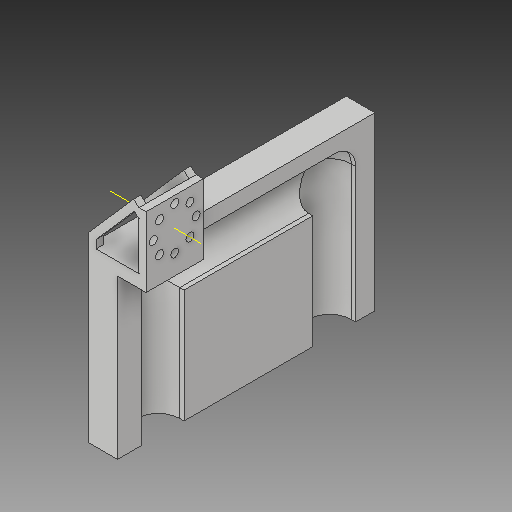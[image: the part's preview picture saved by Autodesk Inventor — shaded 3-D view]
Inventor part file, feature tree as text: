
AUTODESK INVENTOR PART (.ipt)
format: ipt  version: 2019 (Build 230136000, 136)  size: 240,128 bytes
history: native  units: in
note: dims shown in document units (in); Inventor stores cm internally (conversion verified against a paired STEP export)
features: sketch x7, extrude x6, projected_geometry x4, other x2, plane x1, mirror x1, pattern_circular x1, fillet x1
ambient origin geometry x8: Origin, YZ Plane, XZ Plane, XY Plane, X Axis, Y Axis, Z Axis, Center Point
bodies: Solid1 (feature_tree)
feature tree (23):
  other  "relicmold"
  extrude  "Extrusion1"  Depth=4.5in
  extrude  "Extrusion2"  Depth=1.0in
  extrude  "Extrusion3"  Depth=0.125in
  extrude  "Extrusion4"  Depth=0.125in
  plane  "Work Plane1"
  mirror  "Mirror1"
  extrude  "Extrusion5"  Depth=0.125in
  other  "Work Axis1"
  pattern_circular  "Circular Pattern1"  [2 undecoded]
  sketch  "Sketch6"  dims[d14=0.125in d15=0.0in]
  extrude  "Extrusion7"  Depth=1.0in
  fillet  "Fillet2"  Radius=0.5in
  sketch  "Sketch1"  dims[d0=3.0in d1=4.5in]
  sketch  "Sketch2"  dims[d2=0.5in d3=0.0in d4=1.0in]
  sketch  "Sketch3"  dims[d5=0.5in d6=0.0in d8=0.125in]
  projected_geometry  "Projected Loop1"
  sketch  "Sketch4"  dims[d9=1.0in d10=0.0in d11=0.125in]
  sketch  "Sketch5"  dims[d12=0.125in d13=0.125in]
  projected_geometry  "Projected Loop2"
  sketch  "Sketch7"  dims[d16=0.5in d17=1.0in d18=1.0in d19=0.5in d20=0.5in d21=0.14in d22=0.375in d23=0.125in d24=0.0in d25=3.1496in d26=360.0deg d28=0.75in d29=3.0in d30=0.75in d31=0.75in d32=3.75in d36=4.576in d37=0.413in d41=0.45in d42=0.0in d43=0.375in]
  projected_geometry  "Projected Loop3"
  projected_geometry  "Projected Loop4"
note: 2 required parameter values undecoded (feature->parameter linkage not recoverable at this tier; creation-order binding heuristic only, values carry confidence <= 0.55)
